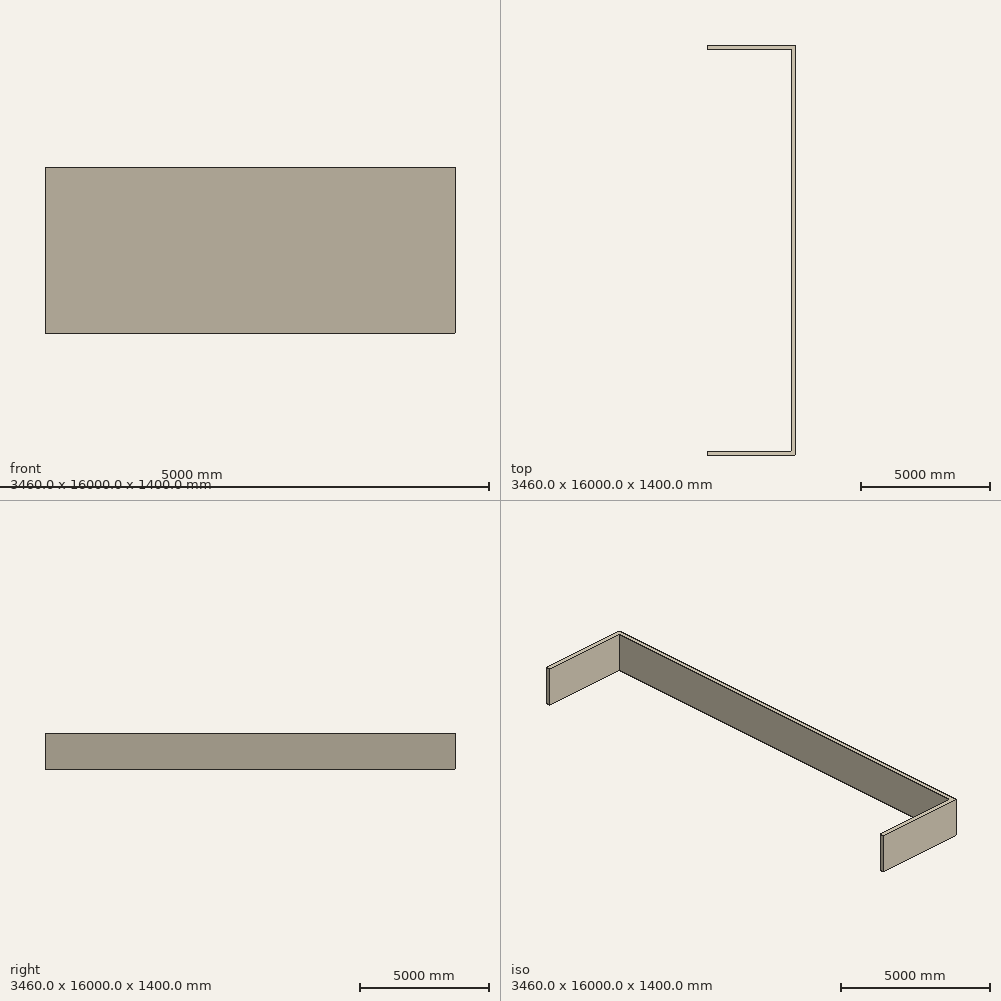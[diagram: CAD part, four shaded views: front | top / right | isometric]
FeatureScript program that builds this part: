
annotation { "Feature Type Name" : "Feature", "Feature Type Description" : "" }
export const myFeature = defineFeature(function(context is Context, id is Id, definition is map)
    precondition{}
    {
        {
            var Q0;
            Q0=qCreatedBy(makeId("Top.planeOp"),FACE);
            var sketch = newSketch(context, id + "F0", { "sketchPlane" : qUnion([Q0])});
            skLineSegment(sketch, "E0", {"start": v(-2397.2, -1250.48) * mm, "end": v(897.8, -1250.48) * mm});
            skLineSegment(sketch, "E1", {"start": v(897.8, -1250.48) * mm, "end": v(897.8, 14419.52) * mm});
            skLineSegment(sketch, "E2", {"start": v(897.8, 14419.52) * mm, "end": v(-2397.2, 14419.52) * mm});
            skLineSegment(sketch, "E3", {"start": v(-2397.2, 14419.52) * mm, "end": v(-2397.2, 14584.52) * mm});
            skLineSegment(sketch, "E4", {"start": v(-2397.2, 14584.52) * mm, "end": v(1062.8, 14584.52) * mm});
            skLineSegment(sketch, "E5", {"start": v(1062.8, 14584.52) * mm, "end": v(1062.8, -1415.48) * mm});
            skLineSegment(sketch, "E6", {"start": v(1062.8, -1415.48) * mm, "end": v(-2397.2, -1415.48) * mm});
            skLineSegment(sketch, "E7", {"start": v(-2397.2, -1415.48) * mm, "end": v(-2397.2, -1250.48) * mm});
            skPoint(sketch, "E8.orphan", {"position": v(62.8, -1415.48) * mm});
            skPoint(sketch, "E9.orphan", {"position": v(1062.8, -415.48) * mm});
            skSolve(sketch);
        }
        {
            var Q0;
            Q0=makeQuery(id+"F0.imprint","IMPRINT",FACE,{"disambiguationData":[TD([[makeQuery(id+"F0.imprint","IMPRINT",EDGE,{"derivedFrom":sQuery(id+"F0.wireOp",EDGE,"E0")}),-1.0]])]});
            extrude(context, id + "F1", {"entities" : qUnion([Q0]), "oppositeDirection" : true, "depth" : 1400 * mm});
        }
    });
